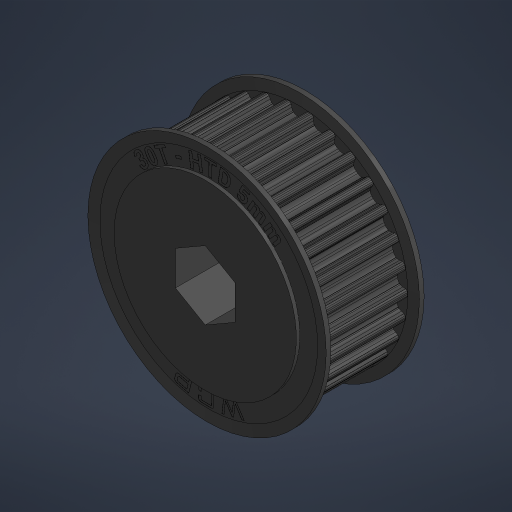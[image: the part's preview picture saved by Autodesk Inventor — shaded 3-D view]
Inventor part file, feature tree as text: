
AUTODESK INVENTOR PART (.ipt)
format: ipt  version: 2023.4 (Build 274418000, 418)  size: 1,144,320 bytes
history: native  units: mm (DEFAULTED — no unit token found)
features: mirror x2, delete_face x1, other x1
ambient origin geometry x8: Origin, YZ Plane, XZ Plane, XY Plane, X Axis, Y Axis, Z Axis, Center Point
bodies: Solid1 (feature_tree), Solid2 (feature_tree), Solid3 (feature_tree)
feature tree (4):
  delete_face  "Delete Face1"
  mirror  "Mirror1"
  mirror  "Mirror1:1"
  other  "Cut-Extrude6"
